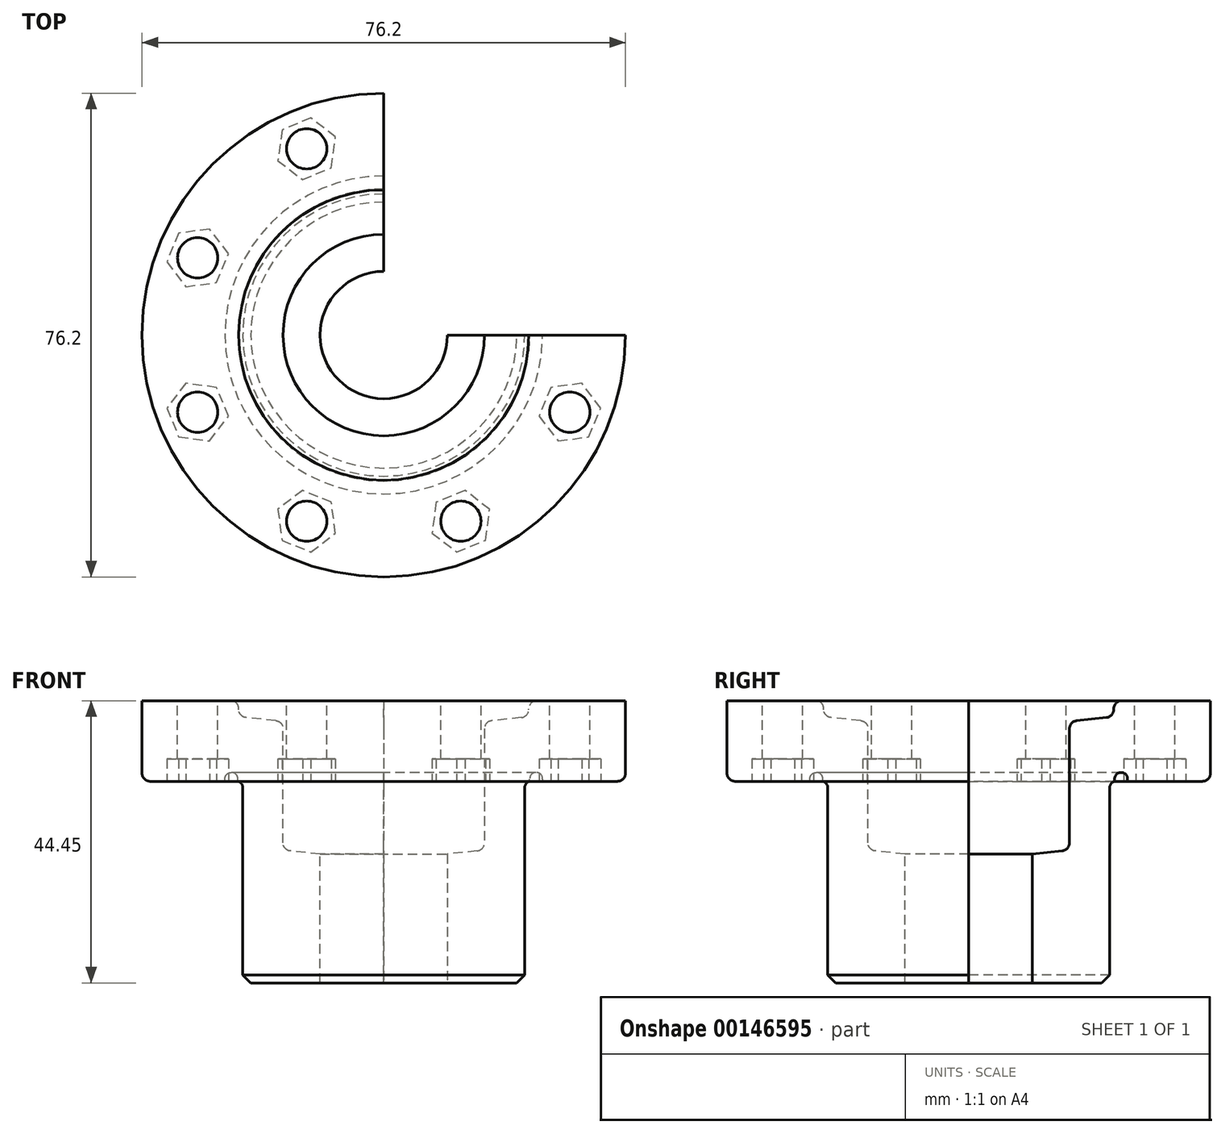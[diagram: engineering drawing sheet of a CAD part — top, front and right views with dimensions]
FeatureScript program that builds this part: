
annotation { "Feature Type Name" : "Feature", "Feature Type Description" : "" }
export const myFeature = defineFeature(function(context is Context, id is Id, definition is map)
    precondition{}
    {
        {
            var Q0;
            Q0=qCreatedBy(makeId("Front.planeOp"),FACE);
            var sketch = newSketch(context, id + "F0", { "sketchPlane" : qUnion([Q0])});
            skLineSegment(sketch, "E0", {"start": v(0, 75.35) * mm, "end": v(0, -76.8) * mm, "construction": true});
            skLineSegment(sketch, "E1", {"start": v(15.88, 69.4) * mm, "end": v(15.88, 49.12) * mm});
            skLineSegment(sketch, "E2", {"start": v(10.03, 48.5) * mm, "end": v(10.03, 28.21) * mm});
            skLineSegment(sketch, "E3", {"start": v(10.03, 28.21) * mm, "end": v(20.96, 28.21) * mm});
            skLineSegment(sketch, "E4", {"start": v(22.23, 29.48) * mm, "end": v(22.23, 59.96) * mm});
            skLineSegment(sketch, "E5", {"start": v(22.86, 70.12) * mm, "end": v(22.86, 72.66) * mm});
            skLineSegment(sketch, "E6", {"start": v(22.86, 72.66) * mm, "end": v(38.1, 72.66) * mm});
            skLineSegment(sketch, "E7", {"start": v(38.1, 72.66) * mm, "end": v(38.1, 59.96) * mm});
            skLineSegment(sketch, "E8", {"start": v(38.1, 59.96) * mm, "end": v(25.03, 59.96) * mm});
            skLineSegment(sketch, "E9", {"start": v(23, 59.96) * mm, "end": v(23, 61.36) * mm});
            skLineSegment(sketch, "E10", {"start": v(23, 61.36) * mm, "end": v(25.03, 61.36) * mm});
            skLineSegment(sketch, "E11", {"start": v(25.03, 61.36) * mm, "end": v(25.03, 59.96) * mm});
            skLineSegment(sketch, "E12.trimOffspring", {"start": v(23, 59.96) * mm, "end": v(22.23, 59.96) * mm});
            skLineSegment(sketch, "E13", {"start": v(20.96, 28.21) * mm, "end": v(22.23, 29.48) * mm});
            skPoint(sketch, "E14.start.orphan", {"position": v(22.23, 28.21) * mm});
            skLineSegment(sketch, "E15", {"start": v(22.86, 70.12) * mm, "end": v(15.88, 69.4) * mm});
            skLineSegment(sketch, "E16", {"start": v(15.88, 49.12) * mm, "end": v(10.03, 48.5) * mm});
            skSolve(sketch);
        }
        {
            var Q0;
            Q0 = qSketchRegion(id + "F0", true);
            var Q1;
            Q1=sQuery(id+"F0.wireOp",EDGE,"E0");
            revolve(context, id + "F1", {"entities" : qUnion([Q0]), "axis" : qUnion([Q1]), "revolveType" : RevolveType.ONE_DIRECTION, "angle" : 270 * degree});
        }
        {
            var Q0;
            Q0=makeQuery(id+"F1.opRevolve","SWEPT_EDGE",EDGE,{"disambiguationData":[OSD([sQuery(id+"F0.wireOp",EDGE,"NfS8FBZc-bgWc-zHHI-cEcd-yeeJX1SY3rAC"),sQuery(id+"F0.wireOp",EDGE,"E5")])]});
            var Q1;
            Q1=makeQuery(id+"F1.opRevolve","SWEPT_EDGE",EDGE,{"disambiguationData":[OSD([sQuery(id+"F0.wireOp",EDGE,"E1"),sQuery(id+"F0.wireOp",EDGE,"bbtoYTUm-32SK-HFDn-8Iwu-w7CrsTeAnLED")])]});
            var Q2;
            Q2=makeQuery(id+"F1.opRevolve","SWEPT_EDGE",EDGE,{"disambiguationData":[OSD([sQuery(id+"F0.wireOp",EDGE,"E7"),sQuery(id+"F0.wireOp",EDGE,"E8")])]});
            fillet(context, id + "F2", {"entities" : qUnion([Q0, Q1, Q2]), "radius" : 1.27 * mm, "tangentPropagation" : true, "allowEdgeOverflow" : false});
        }
        {
            var Q0;
            Q0=makeQuery(id+"F1.opRevolve","SWEPT_EDGE",EDGE,{"disambiguationData":[OSD([sQuery(id+"F0.wireOp",EDGE,"E9"),sQuery(id+"F0.wireOp",EDGE,"E10")])]});
            var Q1;
            Q1=makeQuery(id+"F1.opRevolve","SWEPT_EDGE",EDGE,{"disambiguationData":[OSD([sQuery(id+"F0.wireOp",EDGE,"E10"),sQuery(id+"F0.wireOp",EDGE,"E11")])]});
            var Q2;
            Q2=makeQuery(id+"F1.opRevolve","SWEPT_EDGE",EDGE,{"disambiguationData":[OSD([sQuery(id+"F0.wireOp",EDGE,"E4"),sQuery(id+"F0.wireOp",EDGE,"E12.trimOffspring")])]});
            fillet(context, id + "F3", {"entities" : qUnion([Q0, Q1, Q2]), "radius" : 1.02 * mm, "tangentPropagation" : true, "allowEdgeOverflow" : false});
        }
        {
            var Q0;
            Q0=makeQuery(id+"F1.opRevolve","SWEPT_FACE",FACE,{"disambiguationData":[OSD([sQuery(id+"F0.wireOp",EDGE,"E6")])]});
            var sketch = newSketch(context, id + "F4", { "sketchPlane" : qUnion([Q0])});
            skCircle(sketch, "E17", {"center": v(-12.15, -29.33) * mm, "radius": 3.18 * mm});
            skCircle(sketch, "E18.1.0", {"center": v(12.15, -29.33) * mm, "radius": 3.18 * mm});
            skCircle(sketch, "E18.2.0", {"center": v(29.33, -12.15) * mm, "radius": 3.18 * mm});
            skCircle(sketch, "E18.5.0", {"center": v(-12.15, 29.33) * mm, "radius": 3.18 * mm});
            skCircle(sketch, "E18.6.0", {"center": v(-29.33, 12.15) * mm, "radius": 3.18 * mm});
            skCircle(sketch, "E18.7.0", {"center": v(-29.33, -12.15) * mm, "radius": 3.18 * mm});
            skPoint(sketch, "E18.center", {"position": v(0, 0) * mm});
            skSolve(sketch);
        }
        {
            var Q0;
            Q0=sQuery(id+"F4.wireOp",VERTEX,"E18.2.0.center");
            var Q1;
            Q1=sQuery(id+"F4.wireOp",VERTEX,"E18.1.0.center");
            var Q2;
            Q2=sQuery(id+"F4.wireOp",VERTEX,"E17.center");
            var Q3;
            Q3=sQuery(id+"F4.wireOp",VERTEX,"E18.7.0.center");
            var Q4;
            Q4=sQuery(id+"F4.wireOp",VERTEX,"E18.6.0.center");
            var Q5;
            Q5=sQuery(id+"F4.wireOp",VERTEX,"E18.5.0.center");
            var Q6;
            Q6=makeQuery(id+"F1.opRevolve","SWEPT_BODY",BODY,{"disambiguationData":[OSD([sQuery(id+"F0.wireOp",EDGE,"E1"),sQuery(id+"F0.wireOp",EDGE,"bbtoYTUm-32SK-HFDn-8Iwu-w7CrsTeAnLED"),sQuery(id+"F0.wireOp",EDGE,"E2"),sQuery(id+"F0.wireOp",EDGE,"E3"),sQuery(id+"F0.wireOp",EDGE,"E4"),sQuery(id+"F0.wireOp",EDGE,"NfS8FBZc-bgWc-zHHI-cEcd-yeeJX1SY3rAC"),sQuery(id+"F0.wireOp",EDGE,"E5"),sQuery(id+"F0.wireOp",EDGE,"E6"),sQuery(id+"F0.wireOp",EDGE,"E7"),sQuery(id+"F0.wireOp",EDGE,"E8"),sQuery(id+"F0.wireOp",EDGE,"E9"),sQuery(id+"F0.wireOp",EDGE,"E10"),sQuery(id+"F0.wireOp",EDGE,"E11"),sQuery(id+"F0.wireOp",EDGE,"E12.trimOffspring"),sQuery(id+"F0.wireOp",EDGE,"E13")])]});
            hole(context, id + "F5", {"style" : HoleStyle.SIMPLE, "endStyle" : HoleEndStyle.BLIND, "holeDiameter" : 6.35 * mm, "holeDepth" : 31.75 * mm, "startFromSketch" : true, "locations" : qUnion([Q0, Q1, Q2, Q3, Q4, Q5]), "scope" : qUnion([Q6])});
        }
        {
            var Q0;
            Q0=makeQuery(id+"F1.opRevolve","SWEPT_FACE",FACE,{"disambiguationData":[OSD([sQuery(id+"F0.wireOp",EDGE,"E8")])]});
            var sketch = newSketch(context, id + "F6", { "sketchPlane" : qUnion([Q0])});
            skCircle(sketch, "E19.cCircle", {"center": v(-12.15, -29.33) * mm, "radius": 4.25 * mm, "construction": true});
            skLineSegment(sketch, "E19.0", {"start": v(-12.8, -24.47) * mm, "end": v(-8.26, -26.35) * mm});
            skLineSegment(sketch, "E19.1", {"start": v(-8.26, -26.35) * mm, "end": v(-7.62, -31.21) * mm});
            skLineSegment(sketch, "E19.2", {"start": v(-7.62, -31.21) * mm, "end": v(-11.5, -34.2) * mm});
            skLineSegment(sketch, "E19.3", {"start": v(-11.5, -34.2) * mm, "end": v(-16.04, -32.32) * mm});
            skLineSegment(sketch, "E19.4", {"start": v(-16.04, -32.32) * mm, "end": v(-16.68, -27.46) * mm});
            skLineSegment(sketch, "E19.5", {"start": v(-16.68, -27.46) * mm, "end": v(-12.8, -24.47) * mm});
            skPoint(sketch, "E19.0.midPoint", {"position": v(-10.52, -25.4) * mm});
            skCircle(sketch, "E20.cCircle", {"center": v(-29.33, -12.15) * mm, "radius": 4.25 * mm, "construction": true});
            skLineSegment(sketch, "E20.0", {"start": v(-26.35, -8.26) * mm, "end": v(-24.47, -12.8) * mm});
            skLineSegment(sketch, "E20.1", {"start": v(-24.47, -12.8) * mm, "end": v(-27.46, -16.68) * mm});
            skLineSegment(sketch, "E20.2", {"start": v(-27.46, -16.68) * mm, "end": v(-32.32, -16.04) * mm});
            skLineSegment(sketch, "E20.3", {"start": v(-32.32, -16.04) * mm, "end": v(-34.2, -11.5) * mm});
            skLineSegment(sketch, "E20.4", {"start": v(-34.2, -11.5) * mm, "end": v(-31.21, -7.62) * mm});
            skLineSegment(sketch, "E20.5", {"start": v(-31.21, -7.62) * mm, "end": v(-26.35, -8.26) * mm});
            skPoint(sketch, "E20.0.midPoint", {"position": v(-25.4, -10.52) * mm});
            skCircle(sketch, "E21.cCircle", {"center": v(-29.33, 12.15) * mm, "radius": 4.25 * mm, "construction": true});
            skLineSegment(sketch, "E21.0", {"start": v(-24.47, 12.8) * mm, "end": v(-26.35, 8.26) * mm});
            skLineSegment(sketch, "E21.1", {"start": v(-26.35, 8.26) * mm, "end": v(-31.21, 7.62) * mm});
            skLineSegment(sketch, "E21.2", {"start": v(-31.21, 7.62) * mm, "end": v(-34.2, 11.5) * mm});
            skLineSegment(sketch, "E21.3", {"start": v(-34.2, 11.5) * mm, "end": v(-32.32, 16.04) * mm});
            skLineSegment(sketch, "E21.4", {"start": v(-32.32, 16.04) * mm, "end": v(-27.46, 16.68) * mm});
            skLineSegment(sketch, "E21.5", {"start": v(-27.46, 16.68) * mm, "end": v(-24.47, 12.8) * mm});
            skPoint(sketch, "E21.0.midPoint", {"position": v(-25.4, 10.52) * mm});
            skCircle(sketch, "E22.cCircle", {"center": v(-12.15, 29.33) * mm, "radius": 4.25 * mm, "construction": true});
            skLineSegment(sketch, "E22.0", {"start": v(-8.26, 26.35) * mm, "end": v(-12.8, 24.47) * mm});
            skLineSegment(sketch, "E22.1", {"start": v(-12.8, 24.47) * mm, "end": v(-16.68, 27.46) * mm});
            skLineSegment(sketch, "E22.2", {"start": v(-16.68, 27.46) * mm, "end": v(-16.04, 32.32) * mm});
            skLineSegment(sketch, "E22.3", {"start": v(-16.04, 32.32) * mm, "end": v(-11.5, 34.2) * mm});
            skLineSegment(sketch, "E22.4", {"start": v(-11.5, 34.2) * mm, "end": v(-7.62, 31.21) * mm});
            skLineSegment(sketch, "E22.5", {"start": v(-7.62, 31.21) * mm, "end": v(-8.26, 26.35) * mm});
            skPoint(sketch, "E22.0.midPoint", {"position": v(-10.52, 25.4) * mm});
            skCircle(sketch, "E23.cCircle", {"center": v(12.15, 29.33) * mm, "radius": 4.25 * mm, "construction": true});
            skLineSegment(sketch, "E23.0", {"start": v(12.8, 24.47) * mm, "end": v(8.26, 26.35) * mm});
            skLineSegment(sketch, "E23.1", {"start": v(8.26, 26.35) * mm, "end": v(7.62, 31.21) * mm});
            skLineSegment(sketch, "E23.2", {"start": v(7.62, 31.21) * mm, "end": v(11.5, 34.2) * mm});
            skLineSegment(sketch, "E23.3", {"start": v(11.5, 34.2) * mm, "end": v(16.04, 32.32) * mm});
            skLineSegment(sketch, "E23.4", {"start": v(16.04, 32.32) * mm, "end": v(16.68, 27.46) * mm});
            skLineSegment(sketch, "E23.5", {"start": v(16.68, 27.46) * mm, "end": v(12.8, 24.47) * mm});
            skPoint(sketch, "E23.0.midPoint", {"position": v(10.52, 25.4) * mm});
            skCircle(sketch, "E24.cCircle", {"center": v(29.33, 12.15) * mm, "radius": 4.25 * mm, "construction": true});
            skLineSegment(sketch, "E24.0", {"start": v(26.35, 8.26) * mm, "end": v(24.47, 12.8) * mm});
            skLineSegment(sketch, "E24.1", {"start": v(24.47, 12.8) * mm, "end": v(27.46, 16.68) * mm});
            skLineSegment(sketch, "E24.2", {"start": v(27.46, 16.68) * mm, "end": v(32.32, 16.04) * mm});
            skLineSegment(sketch, "E24.3", {"start": v(32.32, 16.04) * mm, "end": v(34.2, 11.5) * mm});
            skLineSegment(sketch, "E24.4", {"start": v(34.2, 11.5) * mm, "end": v(31.21, 7.62) * mm});
            skLineSegment(sketch, "E24.5", {"start": v(31.21, 7.62) * mm, "end": v(26.35, 8.26) * mm});
            skPoint(sketch, "E24.0.midPoint", {"position": v(25.4, 10.52) * mm});
            skSolve(sketch);
        }
        {
            var Q0;
            Q0 = qSketchRegion(id + "F6", true);
            extrude(context, id + "F7", {"entities" : qUnion([Q0]), "operationType" : NewBodyOperationType.REMOVE, "oppositeDirection" : true, "depth" : 3.5 * mm});
        }
        {
            var Q0;
            Q0 = qSketchRegion(id + "F6", true);
            extrude(context, id + "F8", {"entities" : qUnion([Q0]), "operationType" : NewBodyOperationType.REMOVE, "oppositeDirection" : true, "depth" : 3.5 * mm});
        }
    });
